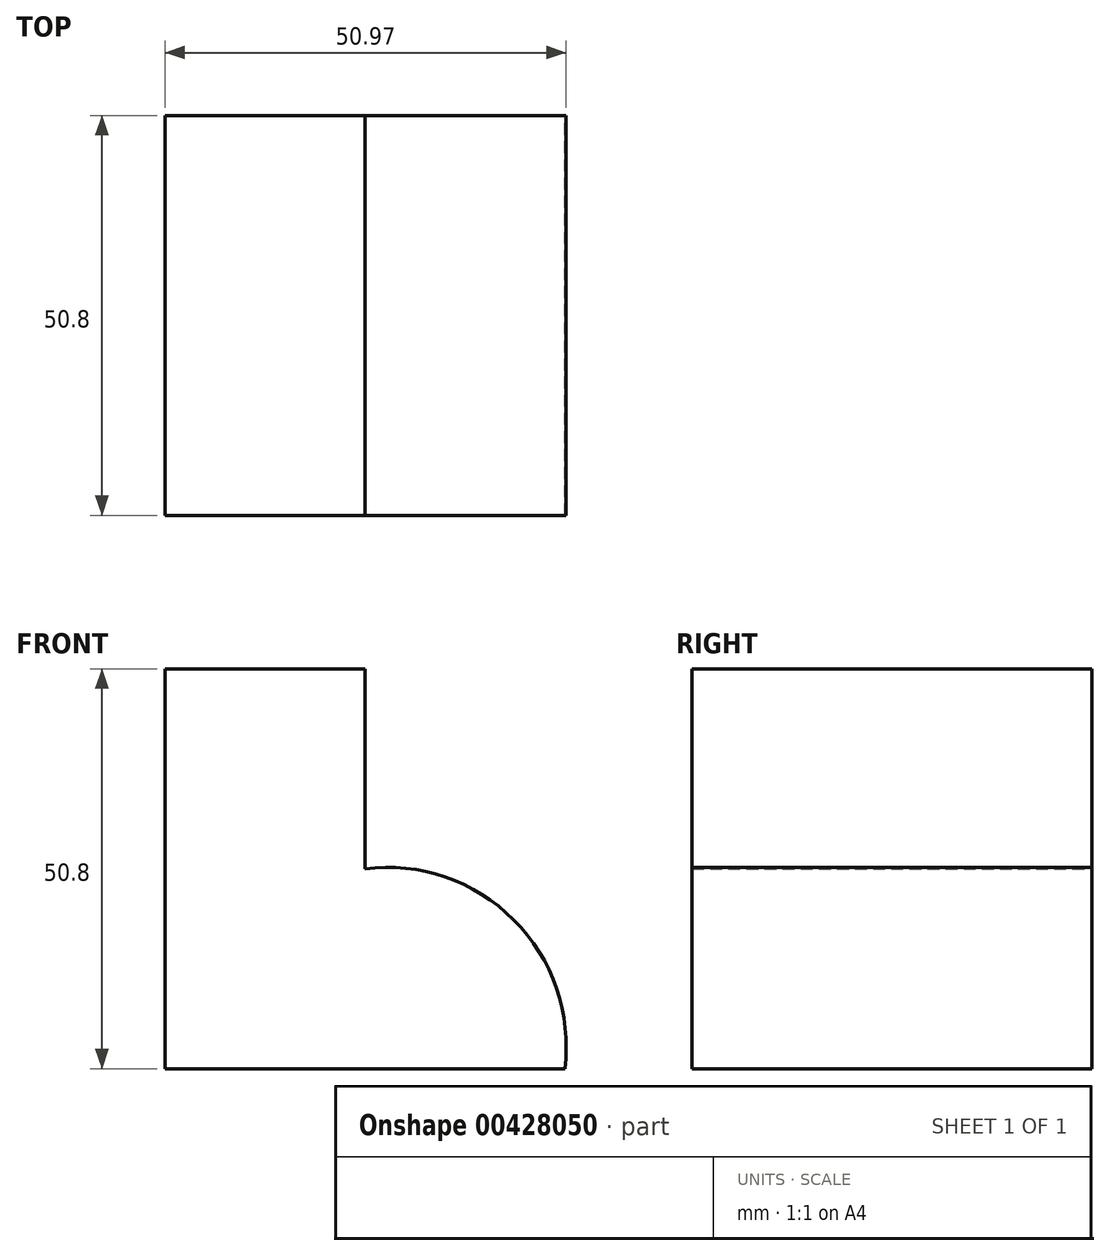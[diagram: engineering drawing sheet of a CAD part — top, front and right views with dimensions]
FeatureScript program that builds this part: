
annotation { "Feature Type Name" : "Feature", "Feature Type Description" : "" }
export const myFeature = defineFeature(function(context is Context, id is Id, definition is map)
    precondition{}
    {
        {
            var Q0;
            Q0=qCreatedBy(makeId("Front.planeOp"),FACE);
            var sketch = newSketch(context, id + "F0", { "sketchPlane" : qUnion([Q0])});
            skLineSegment(sketch, "E0", {"start": v(0, 0) * mm, "end": v(50.8, 0) * mm});
            skLineSegment(sketch, "E1", {"start": v(0, 0) * mm, "end": v(0, 50.8) * mm});
            skLineSegment(sketch, "E2", {"start": v(0, 50.8) * mm, "end": v(25.4, 50.8) * mm});
            skLineSegment(sketch, "E3", {"start": v(25.4, 50.8) * mm, "end": v(25.4, 25.4) * mm});
            skArc(sketch, "E4", {"start": v(50.8, 0) * mm, "mid": v(44.3, 18.9) * mm, "end": v(25.4, 25.4) * mm});
            skSolve(sketch);
        }
        {
            var Q0;
            Q0=makeQuery(id+"F0.imprint","IMPRINT",FACE,{"disambiguationData":[TD([[makeQuery(id+"F0.imprint","IMPRINT",EDGE,{"derivedFrom":sQuery(id+"F0.wireOp",EDGE,"E0")}),1.0]])]});
            extrude(context, id + "F1", {"entities" : qUnion([Q0]), "depth" : 50.8 * mm});
        }
    });
